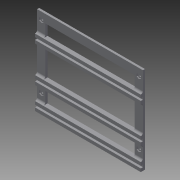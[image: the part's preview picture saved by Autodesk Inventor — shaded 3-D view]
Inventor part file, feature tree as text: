
AUTODESK INVENTOR PART (.ipt)
format: ipt  version: 2014 SP1 (Build 180222100, 222)  size: 209,920 bytes
history: native  units: in
note: dims shown in document units (in); Inventor stores cm internally (conversion verified against a paired STEP export)
features: extrude x7, sketch x7, fillet x1
ambient origin geometry x8: Origin, YZ Plane, XZ Plane, XY Plane, X Axis, Y Axis, Z Axis, Center Point
bodies: Solid1 (feature_tree)
feature tree (15):
  extrude  "Extrusion1"  Depth=5.25in
  extrude  "Extrusion6"  Depth=0.125in TaperAngle=0.0deg
  extrude  "Extrusion7"  Depth=0.13in TaperAngle=0.0deg
  extrude  "Extrusion10"  Depth=0.14in
  sketch  "Sketch15"  dims[d85=0.19in d86=0.19in]
  sketch  "Sketch16"  dims[d87=0.14in d88=0.19in]
  sketch  "Sketch17"  dims[d89=0.19in d90=0.14in d91=0.19in d96=1.215in d98=1.4in d100=0.125in d101=0.0in d102=0.125in d103=0.0in d104=0.125in d105=0.0in d106=0.125in]
  extrude  "Extrusion14"  Depth=0.19in
  extrude  "Extrusion15"  Depth=0.19in
  extrude  "Extrusion16"  Depth=0.14in
  fillet  "Fillet5"  Radius=0.19in
  sketch  "Sketch1"  dims[d0=6.375in d1=5.25in]
  sketch  "Sketch6"  dims[d2=0.125in d3=0.0in d20=0.125in d21=0.0in]
  sketch  "Sketch7"  dims[d22=0.0625in d23=0.0in d74=0.13in d75=0.0in]
  sketch  "Sketch11"  dims[d83=0.19in d84=0.14in]
